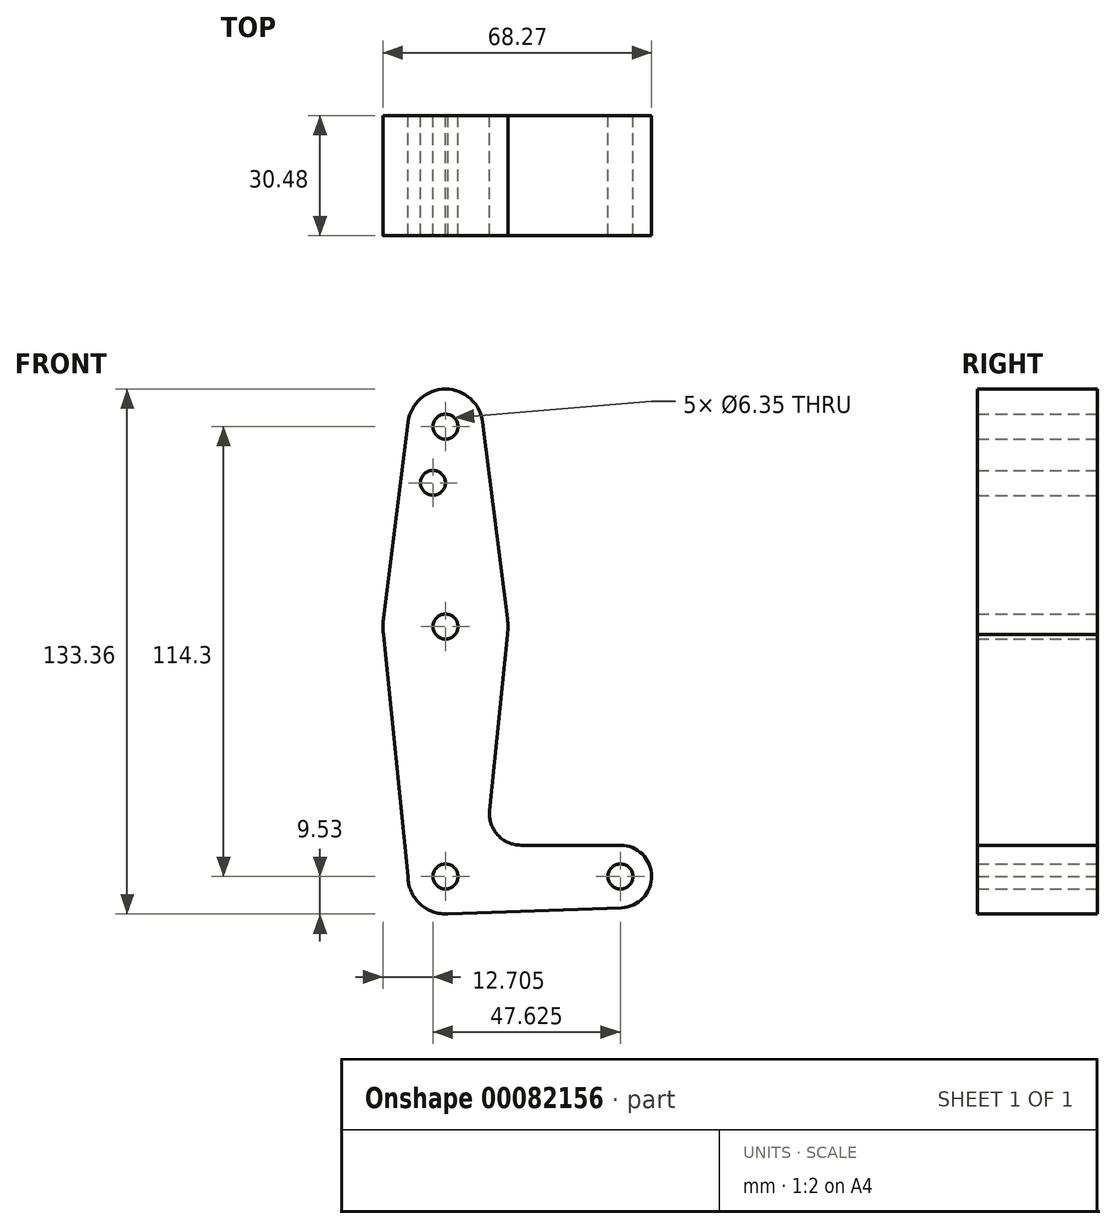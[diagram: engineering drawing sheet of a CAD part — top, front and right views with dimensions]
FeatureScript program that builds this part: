
annotation { "Feature Type Name" : "Feature", "Feature Type Description" : "" }
export const myFeature = defineFeature(function(context is Context, id is Id, definition is map)
    precondition{}
    {
        {
            var Q0;
            Q0=qCreatedBy(makeId("Front.planeOp"),FACE);
            var sketch = newSketch(context, id + "F0", { "sketchPlane" : qUnion([Q0])});
            skLineSegment(sketch, "E0", {"start": v(0, 0) * mm, "end": v(0, 114.3) * mm});
            skLineSegment(sketch, "E1", {"start": v(0, 0) * mm, "end": v(44.45, 0) * mm});
            skCircle(sketch, "E2", {"center": v(0, 0) * mm, "radius": 9.53 * mm});
            skCircle(sketch, "E3", {"center": v(44.45, 0) * mm, "radius": 7.94 * mm});
            skCircle(sketch, "E4", {"center": v(0, 63.5) * mm, "radius": 15.88 * mm});
            skCircle(sketch, "E5", {"center": v(0, 114.3) * mm, "radius": 9.53 * mm});
            skLineSegment(sketch, "E6", {"start": v(-9.46, 115.43) * mm, "end": v(-15.75, 65.48) * mm});
            skLineSegment(sketch, "E7", {"start": v(9.46, 115.43) * mm, "end": v(15.75, 65.48) * mm});
            skLineSegment(sketch, "E8", {"start": v(15.75, 61.52) * mm, "end": v(11.25, 16.68) * mm});
            skLineSegment(sketch, "E9", {"start": v(19.16, 7.94) * mm, "end": v(44.45, 7.94) * mm});
            skLineSegment(sketch, "E10", {"start": v(0, -9.52) * mm, "end": v(44.73, -7.93) * mm});
            skLineSegment(sketch, "E11", {"start": v(-9.52, 0) * mm, "end": v(-15.75, 61.52) * mm});
            skCircle(sketch, "E12", {"center": v(0, 114.3) * mm, "radius": 3.18 * mm});
            skCircle(sketch, "E13", {"center": v(-3.18, 100.03) * mm, "radius": 3.18 * mm});
            skArc(sketch, "E14.filletArc", {"start": v(11.25, 16.68) * mm, "mid": v(13.26, 10.55) * mm, "end": v(19.16, 7.94) * mm});
            skCircle(sketch, "E15", {"center": v(0, 63.5) * mm, "radius": 3.18 * mm});
            skCircle(sketch, "E16", {"center": v(0, 0) * mm, "radius": 3.18 * mm});
            skCircle(sketch, "E17", {"center": v(44.45, 0) * mm, "radius": 3.18 * mm});
            skSolve(sketch);
        }
        {
            var Q0;
            Q0 = qSketchRegion(id + "F0", true);
            var Q1;
            {var subQ0=sQuery(id+"F0.wireOp",EDGE,"E16");var subQ1=sQuery(id+"F0.wireOp",EDGE,"E0");var subQ2=makeQuery(id+"F0.imprint","INTERSECT",VERTEX,{"derivedFrom":[subQ1,subQ0]});Q1=makeQuery(id+"F0.imprint","IMPRINT",FACE,{"disambiguationData":[TD([[makeQuery(id+"F0.imprint","IMPRINT",EDGE,{"disambiguationData":[TD([[subQ2,-1.0]])],"derivedFrom":subQ1}),-1.0]])]});}
            extrude(context, id + "F1", {"entities" : qUnion([Q0, Q1]), "depth" : 30.48 * mm});
        }
    });
